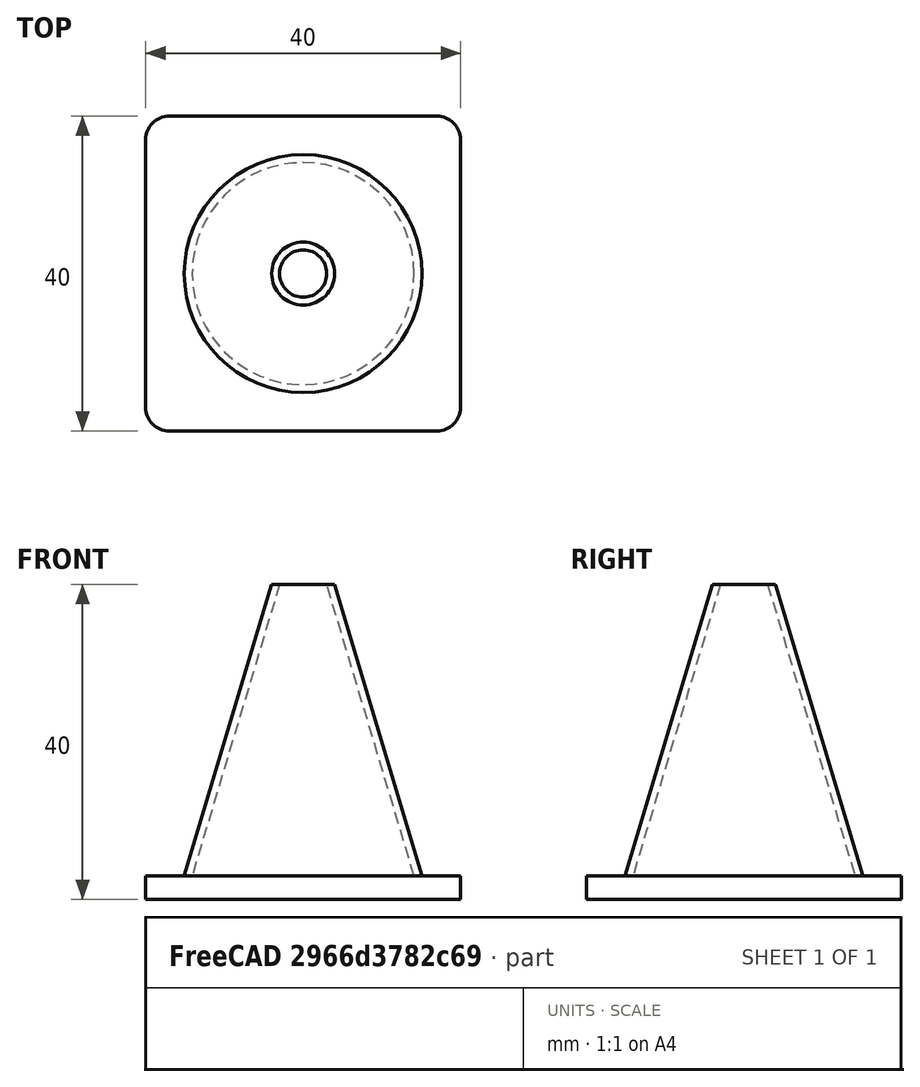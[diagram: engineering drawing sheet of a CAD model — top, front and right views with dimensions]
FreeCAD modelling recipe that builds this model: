
FCSTD DOCUMENT  (FreeCAD 1.0R39319 (Git))
Label: ojt1_t14r02_screw
License: All rights reserved
LicenseURL: https://en.wikipedia.org/wiki/All_rights_reserved
objects: Part::Cone×2, Part::Box×1, Part::Cut×1, Part::Fillet×1, Part::MultiFuse×1
note: 6 computed .brp shape members not serialized (recipe doc carries the construction recipe); baked Part::Feature solids carry a one-line shape summary decoded from their .brp

FEATURE [Part::Box] Box  label="Cub"
  AttacherType = Attacher::AttachEngine3D
  Height = 3
  Length = 40
  Width = 40
FEATURE [Part::Cone] Cone  label="Con"
  Angle = 360
  AttacherType = Attacher::AttachEngine3D
  Height = 40
  Radius1 = 16
  Radius2 = 4
FEATURE [Part::Cone] Cone001  label="Con001"
  Angle = 360
  AttacherType = Attacher::AttachEngine3D
  Height = 40
  Radius1 = 15
  Radius2 = 3
FEATURE [Part::Cut] Cut
  Base = -> Cone
  Placement = pos=(20,20,0) rot=(0,0,1;0rad)
  Refine = true
  Tool = -> Cone001
FEATURE [Part::Fillet] Fillet
  Base = -> Box
  EdgeLinks = -> Box [Edge1,Edge3,Edge5,Edge7]
  Edges = 4 edges r=3: [Edge1,Edge3,Edge5,Edge7]
FEATURE [Part::MultiFuse] Fusion
  Refine = true
  Shapes = -> [Fillet,Cut]
